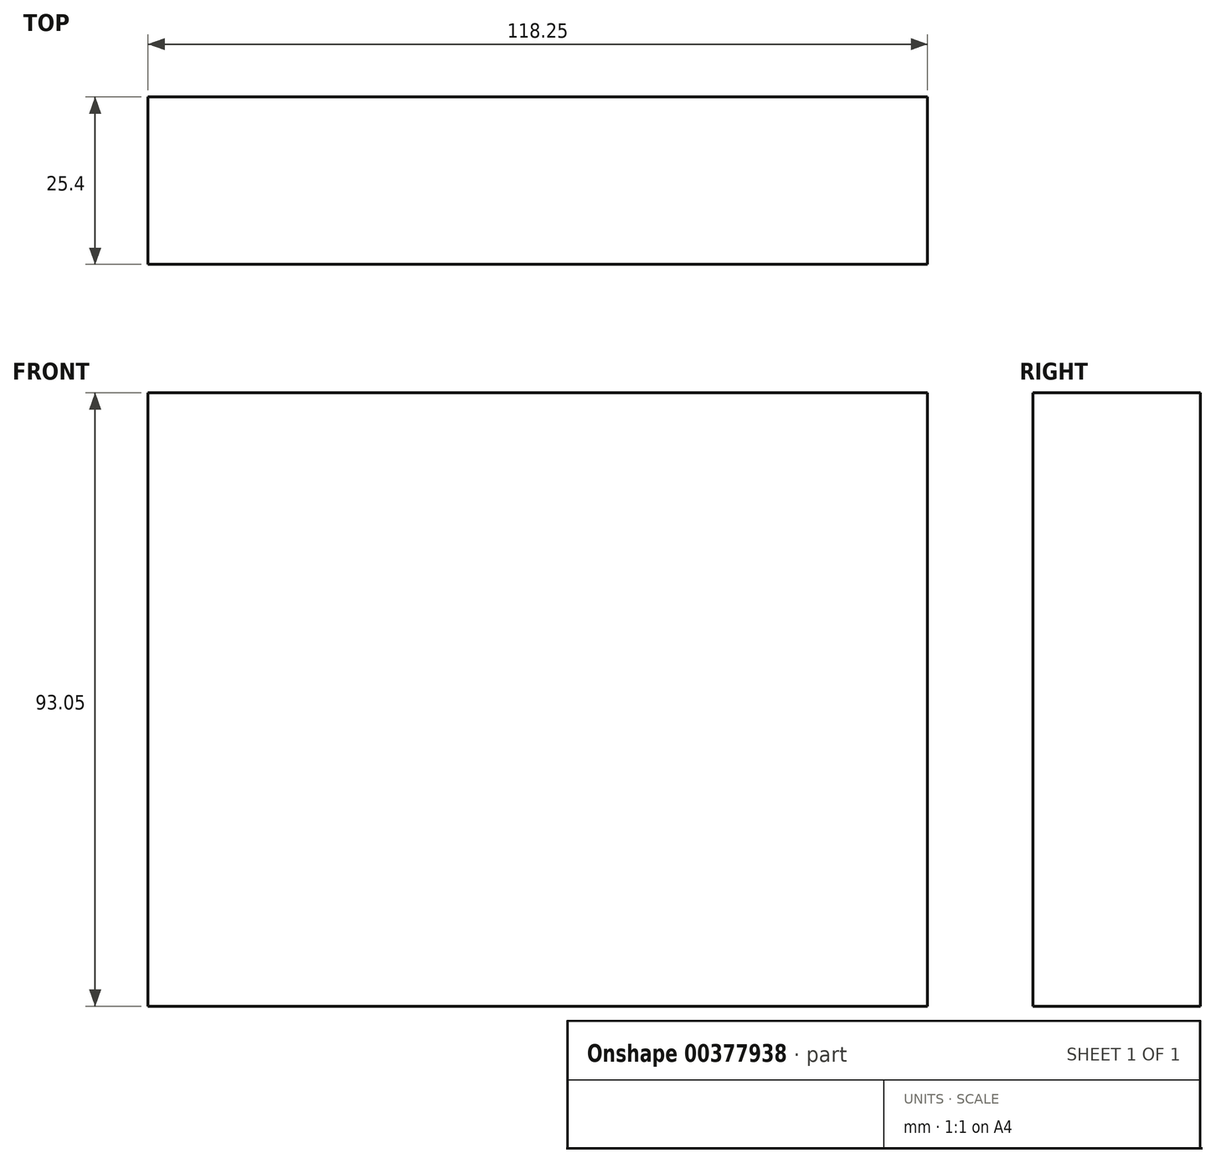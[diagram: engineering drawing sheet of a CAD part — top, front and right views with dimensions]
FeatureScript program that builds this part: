
annotation { "Feature Type Name" : "Feature", "Feature Type Description" : "" }
export const myFeature = defineFeature(function(context is Context, id is Id, definition is map)
    precondition{}
    {
        {
            var Q0;
            Q0=qCreatedBy(makeId("Front.planeOp"),FACE);
            var sketch = newSketch(context, id + "F0", { "sketchPlane" : qUnion([Q0])});
            skLineSegment(sketch, "E0.bottom", {"start": v(45.28, 54.7) * mm, "end": v(-72.97, 54.7) * mm});
            skLineSegment(sketch, "E0.top", {"start": v(45.28, -38.35) * mm, "end": v(-72.97, -38.35) * mm});
            skLineSegment(sketch, "E0.left", {"start": v(45.28, 54.7) * mm, "end": v(45.28, -38.35) * mm});
            skLineSegment(sketch, "E0.right", {"start": v(-72.97, 54.7) * mm, "end": v(-72.97, -38.35) * mm});
            skSolve(sketch);
        }
        {
            var Q0;
            Q0=makeQuery(id+"F0.imprint","IMPRINT",FACE,{"disambiguationData":[TD([[makeQuery(id+"F0.imprint","IMPRINT",EDGE,{"derivedFrom":sQuery(id+"F0.wireOp",EDGE,"E0.bottom")}),1.0]])]});
            extrude(context, id + "F1", {"entities" : qUnion([Q0]), "depth" : 25.4 * mm});
        }
    });
